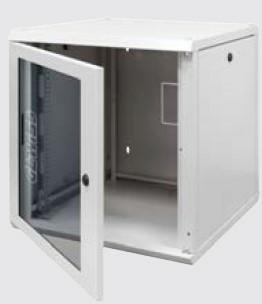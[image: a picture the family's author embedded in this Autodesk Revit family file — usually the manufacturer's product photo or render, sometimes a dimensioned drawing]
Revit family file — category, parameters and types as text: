
# Revit family: Domotics-CablaggioStrutturato-GEWISS-QUADRI_PARETE_19_15U_P600
name_source: partatom
category: Apparecchi elettrici
units: mm (PartAtom-declared; Revit-internal decimal feet)

## family parameters
Condiviso = No
Host = Superficie
Mantenere orientamento annotazione = Sì
Punto di calcolo locali = Sì
Quota connettore circolare = Usa diametro
Taglio con vuoti quando caricato = No
Tipo di parte = Normale

## types (1)
- Domotics-CablaggioStrutturato-GEWISS-QUADRI_PARETE_19_15U_P600
    Apertura porta = 180°
    Catalogo = DOMOTICS
    Categoria = Quadro da parete 19"
    Codice Electrocod = 3752
    Colore = Grigio (RAL 7035)
    Descrizione = QUADRO DA PARETE 19 15U P=600MM.
    Dim. esterne BxHxP (mm) = 600x740x600
    Finitura = Bucciata
    Grado di protezione = IP20
    IDF = ec2be5c7-9306-4a13-a597-c4838f5a08bf
    IDT = 875adcc69f394db3bb3f37c4bdb18b0a
    Immagine tipo = B.jpg
    Materiale = Acciaio
    Modello = GW38419
    N. montanti = 2
    Portata statica = 50KG
    Potenza quadro = 0 V
    Produttore = GEWISS S.p.A.
    Profondità (mm) = 600 mm
    Prospetto di default = 900 mm
    SEO = Quadro
    Scheda Tecnica = https://www.gewiss.com
    Tipologia porta = Reversibile
    URL = https://www.gewiss.com
    Unità di cablaggio = 15 U
    Versione file RFA = 21.2
    n_poli = 1

## geometry (parser evidence)
native form markers: Sweep x4
no freeform markers — native parametric forms only
